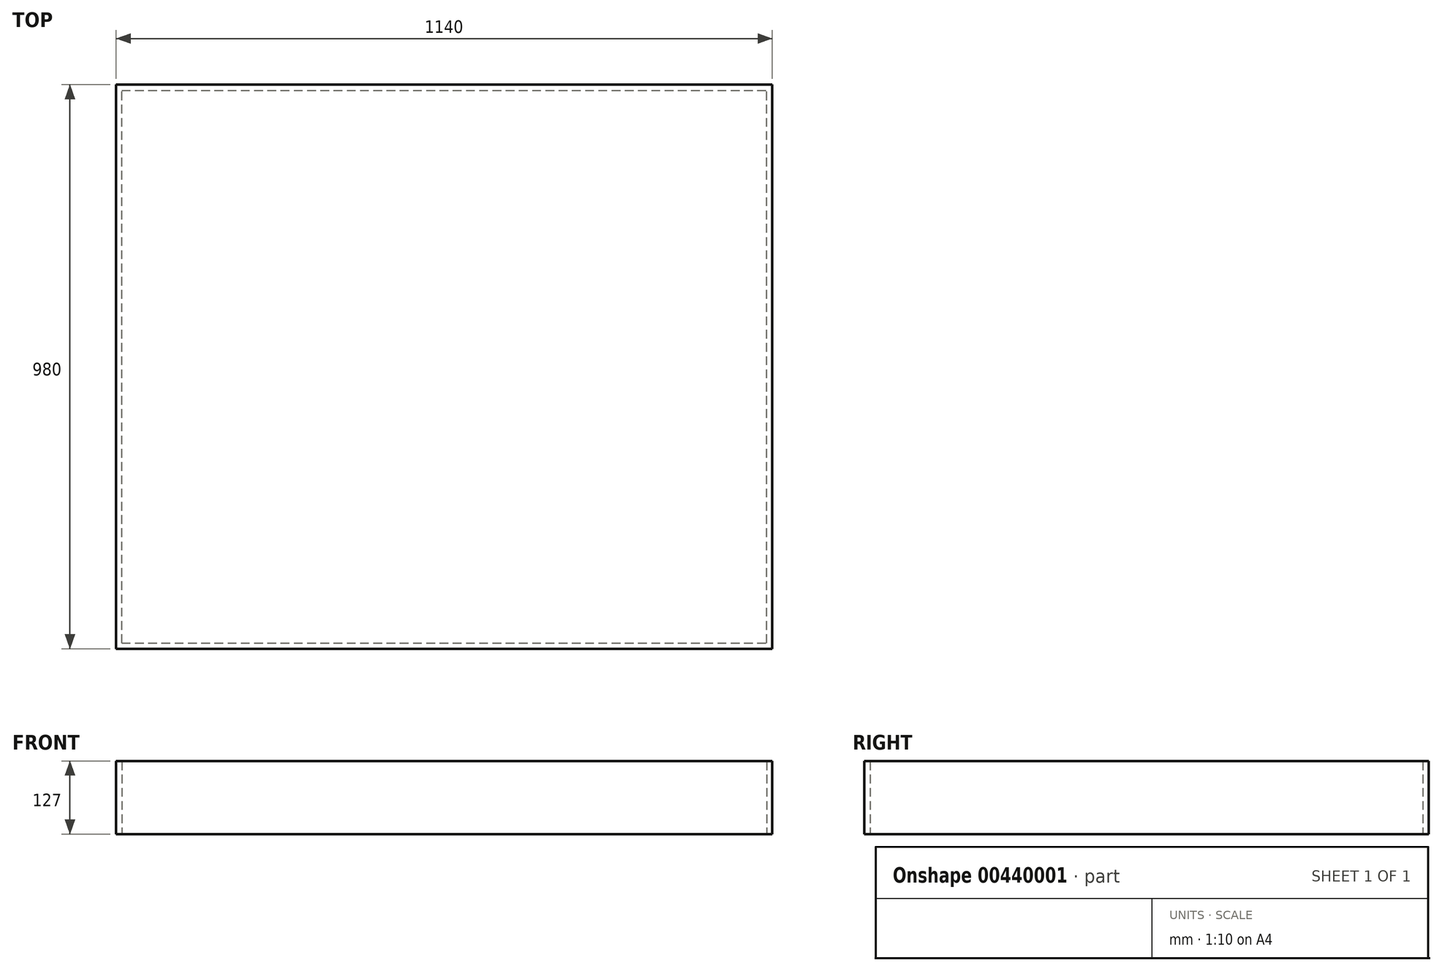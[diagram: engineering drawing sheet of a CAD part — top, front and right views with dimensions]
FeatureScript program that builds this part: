
annotation { "Feature Type Name" : "Feature", "Feature Type Description" : "" }
export const myFeature = defineFeature(function(context is Context, id is Id, definition is map)
    precondition{}
    {
        {
            var Q0;
            Q0=qCreatedBy(makeId("Top.planeOp"),FACE);
            var sketch = newSketch(context, id + "F0", { "sketchPlane" : qUnion([Q0])});
            skLineSegment(sketch, "E0.bottom", {"start": v(-883.69, 494.2) * mm, "end": v(256.31, 494.2) * mm});
            skLineSegment(sketch, "E0.top", {"start": v(-883.69, -485.8) * mm, "end": v(256.31, -485.8) * mm});
            skLineSegment(sketch, "E0.left", {"start": v(-883.69, 494.2) * mm, "end": v(-883.69, -485.8) * mm});
            skLineSegment(sketch, "E0.right", {"start": v(256.31, 494.2) * mm, "end": v(256.31, -485.8) * mm});
            skSolve(sketch);
        }
        {
            var Q0;
            Q0=qSketchRegion(id+"F0",true);
            extrude(context, id + "F1", {"entities" : qUnion([Q0]), "depth" : 127 * mm});
        }
        {
            var Q0;
            Q0=makeQuery(id+"F1.opExtrude","CAP_FACE",FACE,{"disambiguationData":[OSD([sQuery(id+"F0.wireOp",EDGE,"E0.bottom"),sQuery(id+"F0.wireOp",EDGE,"E0.top"),sQuery(id+"F0.wireOp",EDGE,"E0.left"),sQuery(id+"F0.wireOp",EDGE,"E0.right")])],"isStart":true});
            var sketch = newSketch(context, id + "F2", { "sketchPlane" : qUnion([Q0])});
            skLineSegment(sketch, "E1.bottom", {"start": v(-873.69, 475.8) * mm, "end": v(246.31, 475.8) * mm});
            skLineSegment(sketch, "E1.top", {"start": v(-873.69, -484.2) * mm, "end": v(246.31, -484.2) * mm});
            skLineSegment(sketch, "E1.left", {"start": v(-873.69, 475.8) * mm, "end": v(-873.69, -484.2) * mm});
            skLineSegment(sketch, "E1.right", {"start": v(246.31, 475.8) * mm, "end": v(246.31, -484.2) * mm});
            skSolve(sketch);
        }
        {
            var Q0;
            Q0=makeQuery(id+"F2.imprint","IMPRINT",FACE,{"disambiguationData":[TD([[makeQuery(id+"F2.imprint","IMPRINT",EDGE,{"derivedFrom":sQuery(id+"F2.wireOp",EDGE,"E1.bottom")}),-1.0]])]});
            extrude(context, id + "F3", {"entities" : qUnion([Q0]), "operationType" : NewBodyOperationType.REMOVE, "oppositeDirection" : true, "depth" : 126 * mm});
        }
    });
